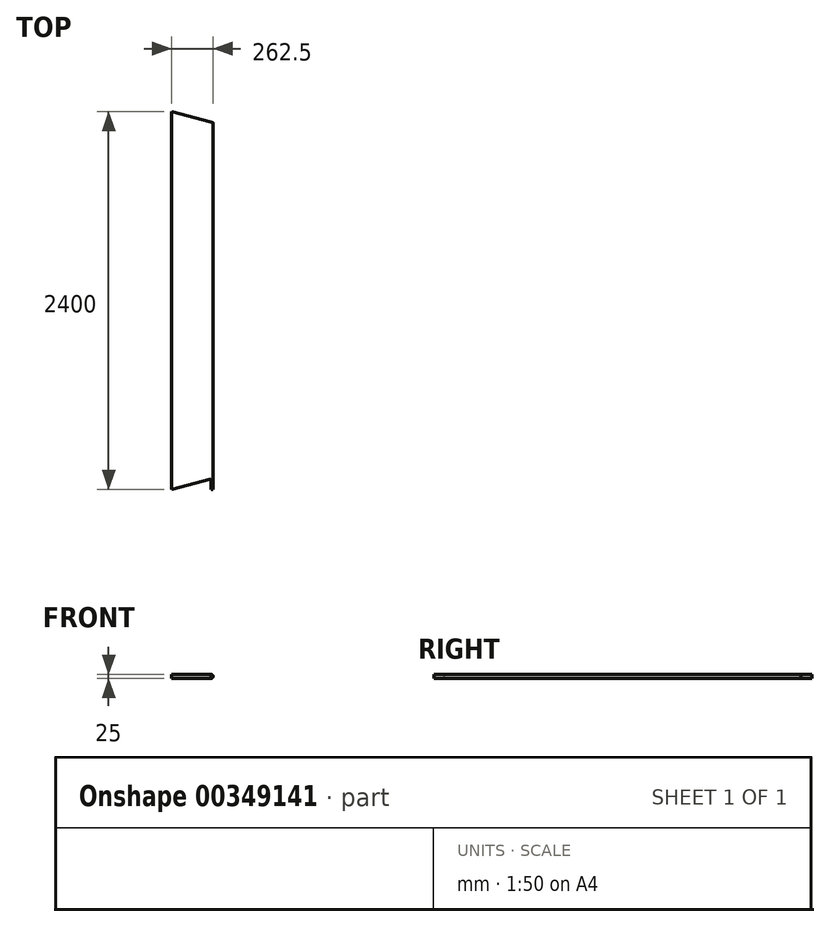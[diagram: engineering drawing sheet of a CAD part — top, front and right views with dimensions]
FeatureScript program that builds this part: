
annotation { "Feature Type Name" : "Feature", "Feature Type Description" : "" }
export const myFeature = defineFeature(function(context is Context, id is Id, definition is map)
    precondition{}
    {
        {
            var Q0;
            Q0=qCreatedBy(makeId("Front.planeOp"),FACE);
            var sketch = newSketch(context, id + "F0", { "sketchPlane" : qUnion([Q0])});
            skLineSegment(sketch, "E0.bottom", {"start": v(0, 0) * mm, "end": v(250, 0) * mm});
            skLineSegment(sketch, "E0.top", {"start": v(0, 25) * mm, "end": v(250, 25) * mm});
            skLineSegment(sketch, "E0.left", {"start": v(0, 0) * mm, "end": v(0, 25) * mm});
            skArc(sketch, "E1", {"start": v(250, 0) * mm, "mid": v(262.5, 12.5) * mm, "end": v(250, 25) * mm});
            skSolve(sketch);
        }
        {
            var Q0;
            Q0=makeQuery(id+"F0.imprint","IMPRINT",FACE,{"disambiguationData":[TD([[makeQuery(id+"F0.imprint","IMPRINT",EDGE,{"derivedFrom":sQuery(id+"F0.wireOp",EDGE,"E0.bottom")}),1.0]])]});
            extrude(context, id + "F1", {"entities" : qUnion([Q0]), "depth" : 2400 * mm});
        }
        {
            var Q0;
            Q0=makeQuery(id+"F1.opExtrude","SWEPT_FACE",FACE,{"disambiguationData":[OSD([sQuery(id+"F0.wireOp",EDGE,"E0.top")])]});
            var sketch = newSketch(context, id + "F2", { "sketchPlane" : qUnion([Q0])});
            skLineSegment(sketch, "E2", {"start": v(262.5, 0) * mm, "end": v(262.5, -2400) * mm});
            skLineSegment(sketch, "E3", {"start": v(0, -2400) * mm, "end": v(262.5, -2329.66) * mm});
            skLineSegment(sketch, "E4", {"start": v(0, 0) * mm, "end": v(262.5, -70.34) * mm});
            skLineSegment(sketch, "E5", {"start": v(0, 0) * mm, "end": v(262.5, 0) * mm});
            skLineSegment(sketch, "E6", {"start": v(0, -2400) * mm, "end": v(262.5, -2400) * mm});
            skLineSegment(sketch, "E7", {"start": v(262.5, -2329.66) * mm, "end": v(262.5, -2400) * mm});
            skSolve(sketch);
        }
        {
            var Q0;
            {var subQ0=sQuery(id+"F2.wireOp",EDGE,"E7");Q0=makeQuery(id+"F2.imprint","IMPRINT",FACE,{"disambiguationData":[TD([[makeQuery(id+"F2.imprint","IMPRINT",EDGE,{"derivedFrom":subQ0}),-1.0]])]});}
            var Q1;
            {var subQ1=sQuery(id+"F2.wireOp",EDGE,"E3");var subQ2=sQuery(id+"F0.wireOp",EDGE,"E0.top");var subQ4=makeQuery(id+"F1.opExtrude","SWEPT_EDGE",EDGE,{"disambiguationData":[OSD([subQ2,sQuery(id+"F0.wireOp",EDGE,"E1")])]});var subQ5=makeQuery(id+"F2.imprint","INTERSECT",VERTEX,{"derivedFrom":[subQ4,subQ1]});Q1=makeQuery(id+"F2.imprint","IMPRINT",FACE,{"disambiguationData":[TD([[makeQuery(id+"F2.imprint","IMPRINT",EDGE,{"disambiguationData":[TD([[subQ5,1.0]])],"derivedFrom":subQ1}),-1.0]])]});}
            var Q2;
            {var subQ1=sQuery(id+"F2.wireOp",EDGE,"E4");var subQ2=sQuery(id+"F0.wireOp",EDGE,"E0.top");var subQ4=makeQuery(id+"F1.opExtrude","SWEPT_EDGE",EDGE,{"disambiguationData":[OSD([subQ2,sQuery(id+"F0.wireOp",EDGE,"E1")])]});var subQ5=makeQuery(id+"F2.imprint","INTERSECT",VERTEX,{"derivedFrom":[subQ4,subQ1]});Q2=makeQuery(id+"F2.imprint","IMPRINT",FACE,{"disambiguationData":[TD([[makeQuery(id+"F2.imprint","IMPRINT",EDGE,{"disambiguationData":[TD([[subQ5,1.0]])],"derivedFrom":subQ1}),1.0]])]});}
            var Q3;
            {var subQ0=sQuery(id+"F2.wireOp",EDGE,"E5");var subQ1=sQuery(id+"F2.wireOp",EDGE,"E2");var subQ2=makeQuery(id+"F2.imprint","INTERSECT",VERTEX,{"derivedFrom":[subQ1,subQ0]});Q3=makeQuery(id+"F2.imprint","IMPRINT",FACE,{"disambiguationData":[TD([[makeQuery(id+"F2.imprint","IMPRINT",EDGE,{"disambiguationData":[TD([[subQ2,-1.0]])],"derivedFrom":subQ1}),-1.0]])]});}
            extrude(context, id + "F3", {"entities" : qUnion([Q0, Q1, Q2, Q3]), "operationType" : NewBodyOperationType.REMOVE, "endBound" : BoundingType.UP_TO_NEXT, "oppositeDirection" : true, "depth" : 25 * mm});
        }
    });
